# Revit family: Поли-Групп_ГидрантПожарный
name_source: partatom
category: Арматура трубопроводов
units: mm (PartAtom-declared; Revit-internal decimal feet)

## family parameters
Всегда вертикально = Да
На основе рабочей плоскости = Нет
Общий = Нет
При загрузке вырезать с полостями = Нет
Размер круглого соединителя = Использовать диаметр
Тип детали = Нормальный

## types (18) — shared parameters
ADSK_URL страницы изделия = https://www.polycorr.ru
ADSK_Версия Revit = 2019
ADSK_Единица измерения = шт.
ADSK_Завод-изготовитель = ООО «КАРБОН»
ADSK_Количество = 1
ADSK_Материал = Ст. 20 (ЭПК цвет синий)
d = 9 мм
h1 = 250 мм
h2 = 25 мм
Группа модели = Арматура трубопроводная
Изображение типоразмера = <Нет>
Климатические условия эксплуатации = У1
Крутящий момент = 105
Материал штока = AISI 201
Покрытие = Порошковая краска ЭПК 64-1-88 ТУ 301-10-0-300-89 (цвет синий)
Пропускная способность = 1.0 м³/ч
Рабочая среда = Питьевая и техническая вода без примесей
Рабочее давление = 10.0 бары
ТВ = ГидрантПожарный_Поли-Групп
Температура рабочей среды = 5 до +70°C
Тип присоединения = Фланцевое

## per-type parameters (varying)
| type | ADSK_Диаметр условный | ADSK_Код изделия | ADSK_Масса | ADSK_Масса_Текст | ADSK_Наименование | ADSK_Наименование краткое | D | D1 | D2 | D3 | DN | H | Габаритные размеры |
| 100-1000 | 100 мм | EAZ-Г1-DN100-1000 | 37 | 37 | Гидрант пожарный подземный EAZ ГП с двойным запиранием DN100-1000 | Гидрант EAZ ГП DN100-1000 | 215 мм | 180 мм | 90 мм | 100 мм | 100 мм | 1000 мм | 215х1000х215 |
| 100-1250 | 100 мм | EAZ-Г1-DN100-1250 | 41 | 41 | Гидрант пожарный подземный EAZ ГП с двойным запиранием DN100-1250 | Гидрант EAZ ГП DN100-1250 | 215 мм | 180 мм | 90 мм | 100 мм | 100 мм | 1250 мм | 215х1250х215 |
| 100-1500 | 100 мм | EAZ-Г1-DN100-1500 | 45 | 45 | Гидрант пожарный подземный EAZ ГП с двойным запиранием DN100-1500 | Гидрант EAZ ГП DN100-1500 | 215 мм | 180 мм | 90 мм | 100 мм | 100 мм | 1500 мм | 215х1500х215 |
| 100-1750 | 100 мм | EAZ-Г1-DN100-1750 | 49 | 49 | Гидрант пожарный подземный EAZ ГП с двойным запиранием DN100-1750 | Гидрант EAZ ГП DN100-1750 | 215 мм | 180 мм | 90 мм | 100 мм | 100 мм | 1750 мм | 215х1750х215 |
| 100-2000 | 100 мм | EAZ-Г1-DN100-1750 | 53 | 53 | Гидрант пожарный подземный EAZ ГП с двойным запиранием DN100-2000 | Гидрант EAZ ГП DN100-2000 | 215 мм | 180 мм | 90 мм | 100 мм | 100 мм | 2000 мм | 215х2000х215 |
| 100-2250 | 100 мм | EAZ-Г1-DN100-2250 | 57 | 57 | Гидрант пожарный подземный EAZ ГП с двойным запиранием DN100-2250 | Гидрант EAZ ГП DN100-2250 | 215 мм | 180 мм | 90 мм | 100 мм | 100 мм | 2250 мм | 215х2250х215 |
| 100-2500 | 100 мм | EAZ-Г1-DN100-2500 | 61 | 61 | Гидрант пожарный подземный EAZ ГП с двойным запиранием DN100-2500 | Гидрант EAZ ГП DN100-2500 | 215 мм | 180 мм | 90 мм | 100 мм | 100 мм | 2500 мм | 215х2500х215 |
| 100-2750 | 100 мм | EAZ-Г1-DN100-2750 | 65 | 65 | Гидрант пожарный подземный EAZ ГП с двойным запиранием DN100-2750 | Гидрант EAZ ГП DN100-2750 | 215 мм | 180 мм | 90 мм | 100 мм | 100 мм | 2750 мм | 215х2750х215 |
| 100-3000 | 100 мм | EAZ-Г1-DN100-3000 | 69 | 69 | Гидрант пожарный подземный EAZ ГП с двойным запиранием DN100-3000 | Гидрант EAZ ГП DN100-3000 | 215 мм | 180 мм | 90 мм | 100 мм | 100 мм | 3000 мм | 215х3000х215 |
| 125-1000 | 125 мм | EAZ-Г1-DN125-1000 | 44 | 44 | Гидрант пожарный подземный EAZ ГП с двойным запиранием DN125-1000 | Гидрант EAZ ГП DN125-1000 | 330 мм | 280 мм | 113 мм | 125 мм | 125 мм | 1000 мм | 330х1000х330 |
| 125-1250 | 125 мм | EAZ-Г1-DN125-1250 | 48 | 48 | Гидрант пожарный подземный EAZ ГП с двойным запиранием DN125-1250 | Гидрант EAZ ГП DN125-1250 | 330 мм | 280 мм | 113 мм | 125 мм | 125 мм | 1250 мм | 330х1250х330 |
| 125-1500 | 125 мм | EAZ-Г1-DN125-1500 | 52 | 52 | Гидрант пожарный подземный EAZ ГП с двойным запиранием DN125-1500 | Гидрант EAZ ГП DN125-1500 | 330 мм | 280 мм | 113 мм | 125 мм | 125 мм | 1500 мм | 330х1500х330 |
| 125-1750 | 125 мм | EAZ-Г1-DN125-1750 | 56 | 56 | Гидрант пожарный подземный EAZ ГП с двойным запиранием DN125-1750 | Гидрант EAZ ГП DN125-1750 | 330 мм | 280 мм | 113 мм | 125 мм | 125 мм | 1750 мм | 330х1750х330 |
| 125-2000 | 125 мм | EAZ-Г1-DN125-2000 | 60 | 60 | Гидрант пожарный подземный EAZ ГП с двойным запиранием DN125-2000 | Гидрант EAZ ГП DN125-2000 | 330 мм | 280 мм | 113 мм | 125 мм | 125 мм | 2000 мм | 330х2000х330 |
| 125-2250 | 125 мм | EAZ-Г1-DN125-2250 | 64 | 64 | Гидрант пожарный подземный EAZ ГП с двойным запиранием DN125-2250 | Гидрант EAZ ГП DN125-2250 | 330 мм | 280 мм | 113 мм | 125 мм | 125 мм | 2250 мм | 330х2250х330 |
| 125-2500 | 125 мм | EAZ-Г1-DN125-2500 | 68 | 68 | Гидрант пожарный подземный EAZ ГП с двойным запиранием DN125-2500 | Гидрант EAZ ГП DN125-2500 | 330 мм | 280 мм | 113 мм | 125 мм | 125 мм | 2500 мм | 330х2500х330 |
| 125-2750 | 125 мм | EAZ-Г1-DN125-2750 | 72 | 72 | Гидрант пожарный подземный EAZ ГП с двойным запиранием DN125-2750 | Гидрант EAZ ГП DN125-2750 | 330 мм | 280 мм | 113 мм | 125 мм | 125 мм | 2750 мм | 330х2750х330 |
| 125-3000 | 125 мм | EAZ-Г1-DN125-3000 | 76 | 76 | Гидрант пожарный подземный EAZ ГП с двойным запиранием DN125-3000 | Гидрант EAZ ГП DN125-3000 | 330 мм | 280 мм | 113 мм | 125 мм | 125 мм | 3000 мм | 330х3000х330 |
